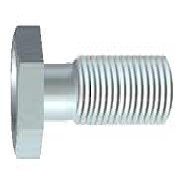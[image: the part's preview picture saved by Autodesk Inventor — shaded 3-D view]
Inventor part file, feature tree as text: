
AUTODESK INVENTOR PART (.ipt)
format: ipt  version: 2018 (Build 220112000, 112)  size: 177,664 bytes
history: native  units: mm (DEFAULTED — no unit token found)
features: sketch x4, extrude x2, chamfer x1, plane x1
ambient origin geometry x7: Origin, YZ Plane, XZ Plane, X Axis, Y Axis, Z Axis, Center Point
bodies: Solid1 (feature_tree), Body (feature_tree)
feature tree (8):
  extrude  "Head"  TaperAngle=90.0deg  [1 undecoded]
  extrude  "Indent"  TaperAngle=0.0deg  [1 undecoded]
  chamfer  "Chamfer1"  Distance=0.39751mm
  plane  "Work Plane1"
  sketch  "Sketch1"  dims[d1=4.1656mm d12=90.0deg]
  sketch  "Sketch2"  dims[d2=2.794mm d3=0.0mm]
  sketch  "Sketch4"  dims[d21=90.0deg d5=0.39751mm d6=0.39761mm d7=0.0mm d8=7.9248mm d9=26.9875mm d10=0.0mm d13=31.75mm d17=7.9248mm d18=6.33984mm d19=0.2804mm d20=0.0mm d77=45.0deg d80=0.0mm d81=0.0mm]
  sketch  "Sketch3"  dims[d4=30.0deg]
note: 2 required parameter values undecoded (feature->parameter linkage not recoverable at this tier; creation-order binding heuristic only, values carry confidence <= 0.55)
